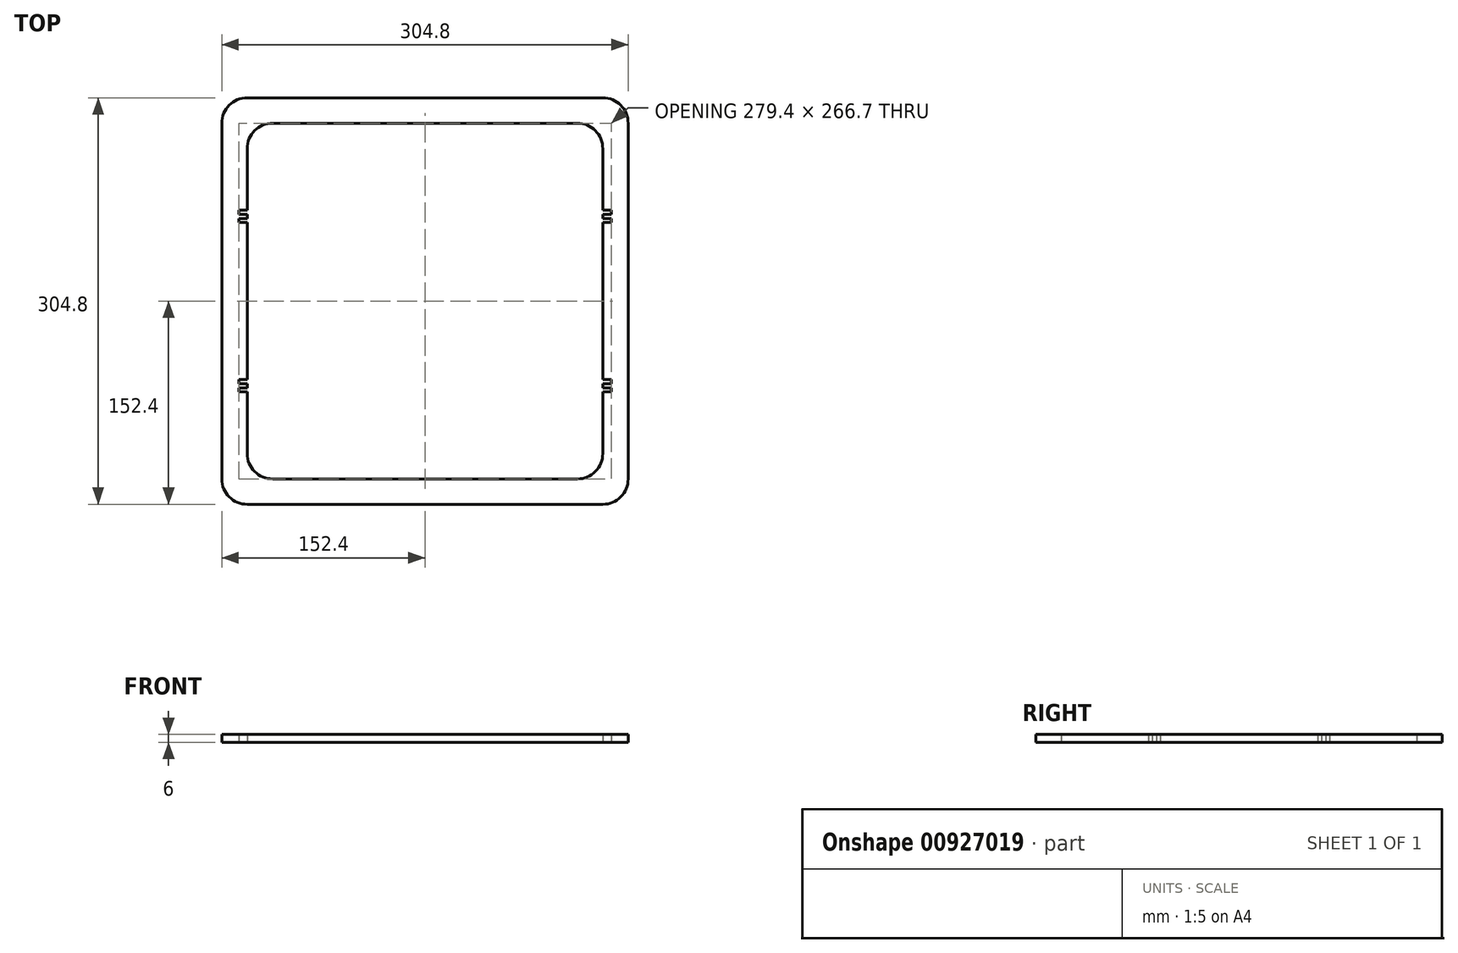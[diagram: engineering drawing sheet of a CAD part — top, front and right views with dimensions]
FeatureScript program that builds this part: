
annotation { "Feature Type Name" : "Feature", "Feature Type Description" : "" }
export const myFeature = defineFeature(function(context is Context, id is Id, definition is map)
    precondition{}
    {
        {
            var Q0;
            Q0=qCreatedBy(makeId("Top.planeOp"),FACE);
            var sketch = newSketch(context, id + "F0", { "sketchPlane" : qUnion([Q0])});
            skLineSegment(sketch, "E0.bottom", {"start": v(0, 0) * mm, "end": v(304.8, 0) * mm});
            skLineSegment(sketch, "E0.top", {"start": v(0, 304.8) * mm, "end": v(304.8, 304.8) * mm});
            skLineSegment(sketch, "E0.left", {"start": v(0, 0) * mm, "end": v(0, 304.8) * mm});
            skLineSegment(sketch, "E0.right", {"start": v(304.8, 0) * mm, "end": v(304.8, 304.8) * mm});
            skLineSegment(sketch, "E1.0", {"start": v(19.05, 285.75) * mm, "end": v(285.75, 285.75) * mm});
            skLineSegment(sketch, "E1.1", {"start": v(19.05, 19.05) * mm, "end": v(19.05, 285.75) * mm});
            skLineSegment(sketch, "E1.2", {"start": v(19.05, 19.05) * mm, "end": v(285.75, 19.05) * mm});
            skLineSegment(sketch, "E1.3", {"start": v(285.75, 19.05) * mm, "end": v(285.75, 285.75) * mm});
            skLineSegment(sketch, "E2.bottom", {"start": v(19.05, 220.49) * mm, "end": v(12.7, 220.49) * mm});
            skLineSegment(sketch, "E2.top", {"start": v(19.05, 217.49) * mm, "end": v(12.7, 217.49) * mm});
            skLineSegment(sketch, "E2.left", {"start": v(19.05, 220.49) * mm, "end": v(19.05, 217.49) * mm});
            skLineSegment(sketch, "E2.right", {"start": v(12.7, 220.49) * mm, "end": v(12.7, 217.49) * mm});
            skLineSegment(sketch, "E3", {"start": v(18.48, 215.9) * mm, "end": v(285.75, 215.9) * mm, "construction": true});
            skLineSegment(sketch, "E4", {"start": v(152.4, 304.8) * mm, "end": v(152.4, 0) * mm, "construction": true});
            skLineSegment(sketch, "E5.MirrorCS", {"start": v(12.7, 211.31) * mm, "end": v(12.7, 214.31) * mm});
            skLineSegment(sketch, "E6.MirrorCS", {"start": v(19.05, 214.31) * mm, "end": v(12.7, 214.31) * mm});
            skLineSegment(sketch, "E7.MirrorCS", {"start": v(19.05, 211.31) * mm, "end": v(12.7, 211.31) * mm});
            skLineSegment(sketch, "E8.MirrorCS", {"start": v(19.05, 211.31) * mm, "end": v(19.05, 214.31) * mm});
            skLineSegment(sketch, "E9.MirrorCS", {"start": v(292.1, 220.49) * mm, "end": v(292.1, 217.49) * mm});
            skLineSegment(sketch, "E10.MirrorCS", {"start": v(285.75, 211.31) * mm, "end": v(285.75, 214.31) * mm});
            skLineSegment(sketch, "E11.MirrorCS", {"start": v(285.75, 220.49) * mm, "end": v(285.75, 217.49) * mm});
            skLineSegment(sketch, "E12.MirrorCS", {"start": v(292.1, 211.31) * mm, "end": v(292.1, 214.31) * mm});
            skLineSegment(sketch, "E13.MirrorCS", {"start": v(285.75, 211.31) * mm, "end": v(292.1, 211.31) * mm});
            skLineSegment(sketch, "E14.MirrorCS", {"start": v(285.75, 217.49) * mm, "end": v(292.1, 217.49) * mm});
            skLineSegment(sketch, "E15.MirrorCS", {"start": v(285.75, 220.49) * mm, "end": v(292.1, 220.49) * mm});
            skLineSegment(sketch, "E16.MirrorCS", {"start": v(285.75, 214.31) * mm, "end": v(292.1, 214.31) * mm});
            skLineSegment(sketch, "E17", {"start": v(19.05, 152.4) * mm, "end": v(285.75, 152.4) * mm, "construction": true});
            skLineSegment(sketch, "E18.MirrorCS", {"start": v(19.05, 87.31) * mm, "end": v(12.7, 87.31) * mm});
            skLineSegment(sketch, "E19.MirrorCS", {"start": v(19.05, 84.31) * mm, "end": v(19.05, 87.31) * mm});
            skLineSegment(sketch, "E20.MirrorCS", {"start": v(292.1, 93.49) * mm, "end": v(292.1, 90.49) * mm});
            skLineSegment(sketch, "E21.MirrorCS", {"start": v(292.1, 84.31) * mm, "end": v(292.1, 87.31) * mm});
            skLineSegment(sketch, "E22.MirrorCS", {"start": v(12.7, 84.31) * mm, "end": v(12.7, 87.31) * mm});
            skLineSegment(sketch, "E23.MirrorCS", {"start": v(19.05, 84.31) * mm, "end": v(12.7, 84.31) * mm});
            skLineSegment(sketch, "E24.MirrorCS", {"start": v(19.05, 93.49) * mm, "end": v(12.7, 93.49) * mm});
            skLineSegment(sketch, "E25.MirrorCS", {"start": v(285.75, 87.31) * mm, "end": v(292.1, 87.31) * mm});
            skLineSegment(sketch, "E26.MirrorCS", {"start": v(285.75, 90.49) * mm, "end": v(292.1, 90.49) * mm});
            skLineSegment(sketch, "E27.MirrorCS", {"start": v(12.7, 93.49) * mm, "end": v(12.7, 90.49) * mm});
            skLineSegment(sketch, "E28.MirrorCS", {"start": v(285.75, 84.31) * mm, "end": v(285.75, 87.31) * mm});
            skLineSegment(sketch, "E29.MirrorCS", {"start": v(285.75, 93.49) * mm, "end": v(285.75, 90.49) * mm});
            skLineSegment(sketch, "E30.MirrorCS", {"start": v(19.05, 93.49) * mm, "end": v(19.05, 90.49) * mm});
            skLineSegment(sketch, "E31.MirrorCS", {"start": v(285.75, 93.49) * mm, "end": v(292.1, 93.49) * mm});
            skLineSegment(sketch, "E32.MirrorCS", {"start": v(19.05, 90.49) * mm, "end": v(12.7, 90.49) * mm});
            skLineSegment(sketch, "E33.MirrorCS", {"start": v(285.75, 84.31) * mm, "end": v(292.1, 84.31) * mm});
            skLineSegment(sketch, "E34.MirrorCS", {"start": v(18.48, 88.9) * mm, "end": v(285.75, 88.9) * mm, "construction": true});
            skSolve(sketch);
        }
        {
            var Q0;
            Q0=makeQuery(id+"F0.imprint","IMPRINT",FACE,{"disambiguationData":[TD([[makeQuery(id+"F0.imprint","IMPRINT",EDGE,{"derivedFrom":sQuery(id+"F0.wireOp",EDGE,"E0.bottom")}),1.0]])]});
            extrude(context, id + "F1", {"entities" : qUnion([Q0]), "depth" : 6 * mm, "offsetDistance" : 25.4 * mm});
        }
        {
            var Q0;
            Q0=makeQuery(id+"F1.opExtrude","SWEPT_EDGE",EDGE,{"disambiguationData":[OSD([sQuery(id+"F0.wireOp",EDGE,"E1.0"),sQuery(id+"F0.wireOp",EDGE,"E1.1")])]});
            var Q1;
            Q1=makeQuery(id+"F1.opExtrude","SWEPT_EDGE",EDGE,{"disambiguationData":[OSD([sQuery(id+"F0.wireOp",EDGE,"E1.0"),sQuery(id+"F0.wireOp",EDGE,"E1.3")])]});
            var Q2;
            Q2=makeQuery(id+"F1.opExtrude","SWEPT_EDGE",EDGE,{"disambiguationData":[OSD([sQuery(id+"F0.wireOp",EDGE,"E1.2"),sQuery(id+"F0.wireOp",EDGE,"E1.3")])]});
            var Q3;
            Q3=makeQuery(id+"F1.opExtrude","SWEPT_EDGE",EDGE,{"disambiguationData":[OSD([sQuery(id+"F0.wireOp",EDGE,"E1.1"),sQuery(id+"F0.wireOp",EDGE,"E1.2")])]});
            var Q4;
            Q4=makeQuery(id+"F1.opExtrude","SWEPT_EDGE",EDGE,{"disambiguationData":[OSD([sQuery(id+"F0.wireOp",EDGE,"E0.bottom"),sQuery(id+"F0.wireOp",EDGE,"E0.right")])]});
            var Q5;
            Q5=makeQuery(id+"F1.opExtrude","SWEPT_EDGE",EDGE,{"disambiguationData":[OSD([sQuery(id+"F0.wireOp",EDGE,"E0.top"),sQuery(id+"F0.wireOp",EDGE,"E0.right")])]});
            var Q6;
            Q6=makeQuery(id+"F1.opExtrude","SWEPT_EDGE",EDGE,{"disambiguationData":[OSD([sQuery(id+"F0.wireOp",EDGE,"E0.top"),sQuery(id+"F0.wireOp",EDGE,"E0.left")])]});
            var Q7;
            Q7=makeQuery(id+"F1.opExtrude","SWEPT_EDGE",EDGE,{"disambiguationData":[OSD([sQuery(id+"F0.wireOp",EDGE,"E0.bottom"),sQuery(id+"F0.wireOp",EDGE,"E0.left")])]});
            fillet(context, id + "F2", {"entities" : qUnion([Q0, Q1, Q2, Q3, Q4, Q5, Q6, Q7]), "radius" : 19.05 * mm, "tangentPropagation" : true, "allowEdgeOverflow" : false});
        }
    });
